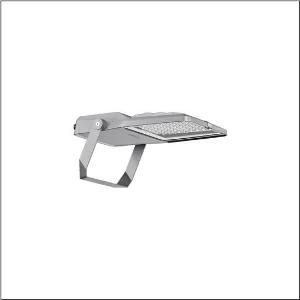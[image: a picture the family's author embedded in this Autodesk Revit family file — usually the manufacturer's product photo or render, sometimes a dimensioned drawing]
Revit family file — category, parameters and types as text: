
# Revit family: floodlight_fl_21_mini___pl61_5xa7776c2c1a_8570
name_source: partatom
category: Lighting Fixtures
units: mm (PartAtom-declared; Revit-internal decimal feet)

## family parameters
Cut with Voids When Loaded = No
Host = Face
Light Source = No
Part Type = Normal
Room Calculation Point = No
Round Connector Dimension = Use Diameter
Shared = No

## types (1)
- --- (1 x LED, 11960 lm, 89 W, 3000K)
    Apparent Load = 89 VA
    CIE Flux Codes = 33 65 98 100 100
    Color Rendering = 70
    Color Temperature = 3000K
    Default Elevation = 1800 mm
    Description = Floodlight FL 21 mini, floodlight, primary light control with lens, of PMMA, primary optical cover: protective disc, of toughened safety glass, transparent, light distribution: PL61, light emission: direct distribution, installation type: surface-mounted, LED, High Power LED, rated luminous flux: 11.960lm, luminous efficacy: 134lm/W, light colour: 730, colour temperature: 3000K, control: flexible luminous flux parameterisation, time-dependent luminous flux control, constant luminous flux control, overheat protection, presetting dimming logarithmic, with terminal, 6-pole, mains connection: 220..240V, AC, 50/60Hz, start of lifetime: 89W, end of service life: 94W, reduction: 43W, luminaire housing, of diecast aluminium, powder-coated, Siteco® metallic grey (DB 702S), corrosivity category C5 mid according to DIN EN ISO 12944, sealing non-destructively replaceable, mounting bracket, of steel, galvanised, powder-coated, Siteco® metallic grey (DB 702S), Smart Interface below and above, protection rating (complete): IP66, insulation class (complete): insulation class II (safety insulation), certification: CE, ENEC, VDE, protection symbol: D, impact resistance: IK08, permissible operating ambient temperature: -40..+40°C, permissible operating ambient temperature for outdoor applications: -40..+50°C, standard: DIN EN 12944, LABS conformity tested according to VDMA 24364:2018-05, packaging unit: 1 piece

Light Distribution: PL61
    Height = 70 mm
    Lamp = 1 x LED
    Lamp Light Flux = 11960 lm
    Lamp Power = 89 W
    Lamp count = 1
    Length = 485 mm
    Luminous efficacy = 134 lm/W
    Manufacturer = Siteco
    ModVariant = No
    Model = 5XA7776C2C1A
    Number of Poles = 1
    OnlyDefault = Yes
    Power Factor = 1
    Product Name = Floodlight FL 21 mini | PL61
    Product group = floodlight | pylon annexe
    ProductGroupID = 6200
    Protection Class = Protection class II
    Protection Degree = IP 66
    RLX_Detail_Level = 1
    RLX_Emergency_Light_Flux = 0 lm
    RLX_Emergency_Type = 0
    RLX_Emergency_Type_DB = No
    RlxData = <blob elided: 95845 chars, md5=d127fc2d>
    Socket = socket
    Standby Power = 0 W
    System Light Flux = 11960 lm
    System Power = 89 W
    Type Comments = factory setting: luminous flux: 100 % | dim-lin: 254 | 456 mA
    Type Image = l_1006845.jpg
    URL = http://relux.com
    VarID = @adj_105105
    Voltage = 0 V
    Weight = 0.00 kg
    Width = 337 mm

## geometry (parser evidence)
native form markers: Blend x4, Sweep x14
no freeform markers — native parametric forms only
